# Revit family: Eurolan_Полка стационарная
name_source: partatom
category: Устройства связи
units: mm (PartAtom-declared; Revit-internal decimal feet)

## family parameters
Всегда вертикально = Да
На основе рабочей плоскости = Нет
Общий = Нет
При загрузке вырезать с полостями = Нет
Размер круглого соединителя = Использовать диаметр
Сохранять ориентацию аннотаций = Нет
Тип детали = Нормальный
Точка расчета площади = Нет

## types (11) — shared parameters
ADSK_Единица измерения = шт
ADSK_Завод-изготовитель = Eurolan
ADSK_Количество = 1
ADSK_Материал = Черный антрацит

## per-type parameters (varying)
| type | ADSK_Код изделия | ADSK_Марка | ADSK_Масса | ADSK_Наименование | ADSK_Наименование краткое | Выбор_геометрии |
| Полка стационарная до 50 кг_глубина 390 мм | 60A-01-39-11BL | 50 | 2.1 | Полка стационарная до 50 кг, глубина 390 мм | Полка стационарная до 50 кг, | Полка стационарная 1U _без_регул.кронштейна : 390 |
| Полка стационарная до 50 кг_глубина 450 мм | 60A-01-45-11BL | 50 | 2.4 | Полка стационарная до 50 кг, глубина 450 мм | Полка стационарная до 50 кг | Полка стационарная 1U _без_регул.кронштейна : 450 |
| Полка стационарная до 50 кг_глубина 580 мм | 60A-01-58-11BL | 50 | 2.95 | Полка стационарная до 50 кг, глубина 580 мм | Полка стационарная до 50 кг | Полка стационарная 1U _без_регул.кронштейна : 580 |
| Полка стационарная до 50 кг_глубина 620 мм | 60A-01-62-11BL | 50 | 3.15 | Полка стационарная до 50 кг, глубина 620 мм | Полка стационарная до 50 кг | Полка стационарная 1U _без_регул.кронштейна : 620 |
| Полка стационарная до 50 кг_глубина 750 мм | 60A-01-75-11BL | 50 | 3.73 | Полка стационарная до 50 кг, глубина 750 мм | Полка стационарная до 50 кг | Полка стационарная 1U _без_регул.кронштейна : 750 |
| Полка стационарная до 50 кг_глубина 1000 мм | 60A-01-1A-11BL | 50 | 4.86 | Полка стационарная до 50 кг, глубина 1000 мм | Полка стационарная до 50 кг | Полка стационарная 1U _без_регул.кронштейна : 1000 |
| Полка стационарная до 100 кг_глубина 450 мм | 60A-01-45-12BL | 100 | 3.2 | Полка стационарная до 100 кг, глубина 450 мм | Полка стационарная до 100 кг | Полка стационарная 1U _без_регул.кронштейна : 450 |
| Полка стационарная до 100 кг_глубина 580 мм | 60A-01-58-12BL | 100 | 3.9 | Полка стационарная до 100 кг, глубина 580 мм | Полка стационарная до 100 кг | Полка стационарная 1U _без_регул.кронштейна : 580 |
| Полка стационарная до 100 кг_глубина 620 мм | 60A-01-62-12BL | 100 | 4.1 | Полка стационарная до 100 кг, глубина 620 мм | Полка стационарная до 100 кг | Полка стационарная 1U _без_регул.кронштейна : 620 |
| Полка стационарная до 100 кг_глубина 750 мм | 60A-01-75-12BL | 100 | 5.5 | Полка стационарная до 100 кг, глубина 750 мм | Полка стационарная до 100 кг | Полка стационарная 1U _без_регул.кронштейна : 750 |
| Полка стационарная до 100 кг_глубина 1000 мм | 60A-01-1А-12BL | 100 | 7.9 | Полка стационарная до 100 кг, глубина 1000 мм | Полка стационарная до 100 кг | Полка стационарная 1U _без_регул.кронштейна : 1000 |
